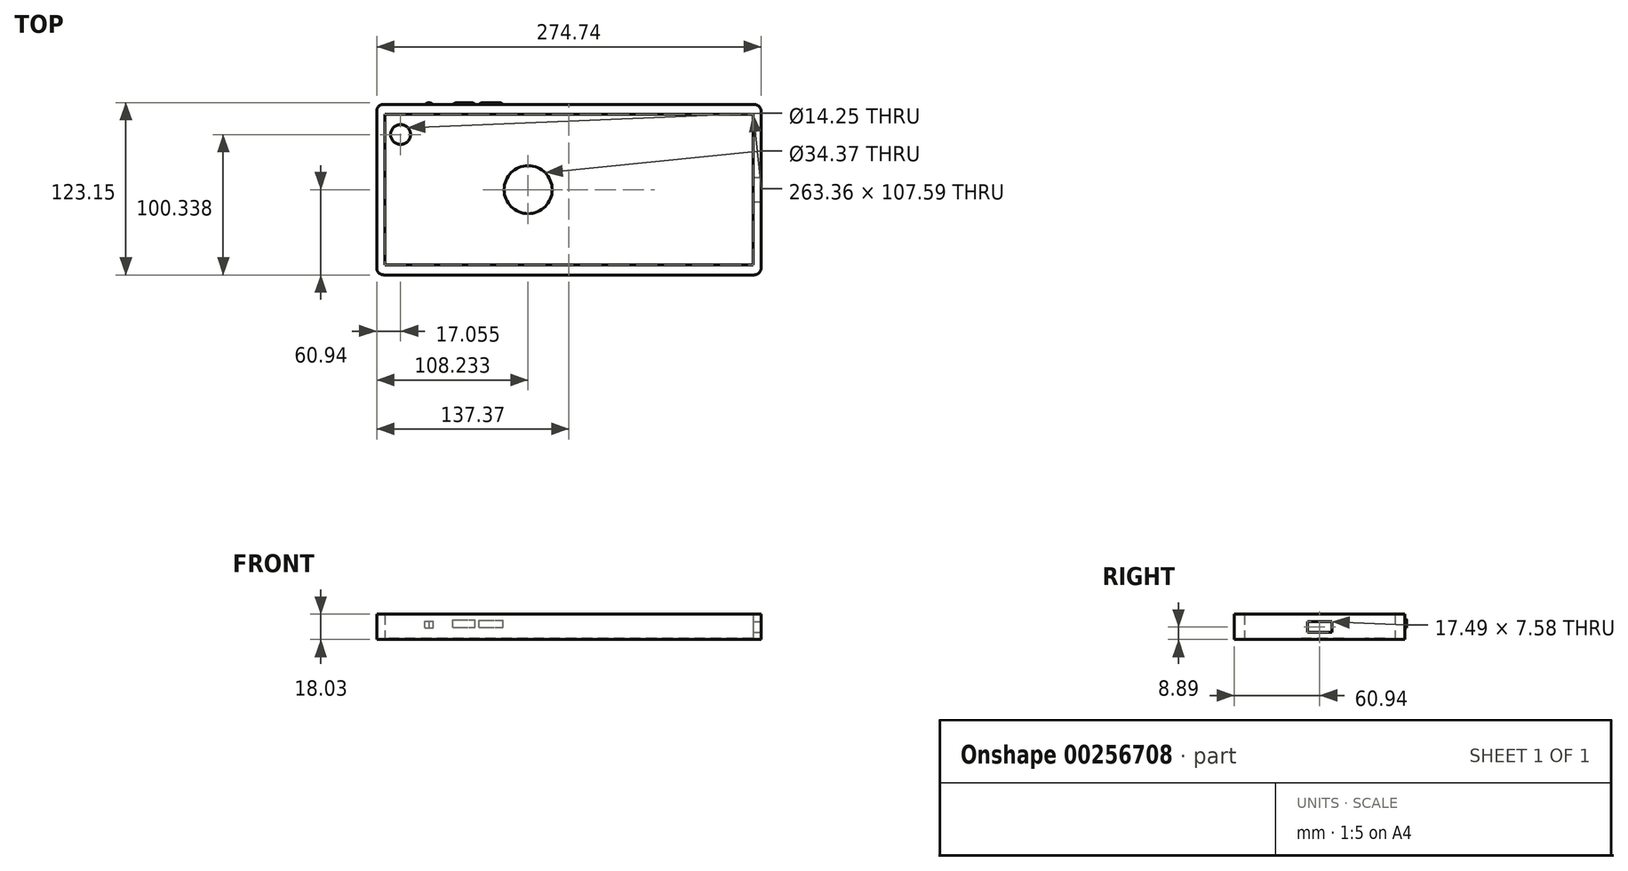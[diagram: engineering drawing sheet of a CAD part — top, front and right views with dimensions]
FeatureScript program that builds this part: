
annotation { "Feature Type Name" : "Feature", "Feature Type Description" : "" }
export const myFeature = defineFeature(function(context is Context, id is Id, definition is map)
    precondition{}
    {
        {
            var Q0;
            Q0=qCreatedBy(makeId("Top.planeOp"),FACE);
            var sketch = newSketch(context, id + "F0", { "sketchPlane" : qUnion([Q0])});
            skLineSegment(sketch, "E0.bottom", {"start": v(137.37, -60.94) * mm, "end": v(-137.37, -60.94) * mm});
            skLineSegment(sketch, "E0.top", {"start": v(137.37, 60.94) * mm, "end": v(-137.37, 60.94) * mm});
            skLineSegment(sketch, "E0.left", {"start": v(137.37, -60.94) * mm, "end": v(137.37, 60.94) * mm});
            skLineSegment(sketch, "E0.right", {"start": v(-137.37, -60.94) * mm, "end": v(-137.37, 60.94) * mm});
            skPoint(sketch, "E0.middle", {"position": v(0, 0) * mm});
            skLineSegment(sketch, "E1.bottom", {"start": v(131.68, -53.8) * mm, "end": v(-131.68, -53.8) * mm});
            skLineSegment(sketch, "E1.top", {"start": v(131.68, 53.8) * mm, "end": v(-131.68, 53.8) * mm});
            skLineSegment(sketch, "E1.left", {"start": v(131.68, -53.8) * mm, "end": v(131.68, 53.8) * mm});
            skLineSegment(sketch, "E1.right", {"start": v(-131.68, -53.8) * mm, "end": v(-131.68, 53.8) * mm});
            skSolve(sketch);
        }
        {
            var Q0;
            Q0 = qSketchRegion(id + "F0", true);
            extrude(context, id + "F1", {"entities" : qUnion([Q0]), "depth" : 18.03 * mm});
        }
        {
            var Q0;
            Q0=makeQuery(id+"F1.opExtrude","CAP_FACE",FACE,{"disambiguationData":[OSD([sQuery(id+"F0.wireOp",EDGE,"E0.bottom"),sQuery(id+"F0.wireOp",EDGE,"E0.top"),sQuery(id+"F0.wireOp",EDGE,"E0.left"),sQuery(id+"F0.wireOp",EDGE,"E0.right"),sQuery(id+"F0.wireOp",EDGE,"E1.bottom"),sQuery(id+"F0.wireOp",EDGE,"E1.top"),sQuery(id+"F0.wireOp",EDGE,"E1.left"),sQuery(id+"F0.wireOp",EDGE,"E1.right")])],"isStart":true});
            var sketch = newSketch(context, id + "F2", { "sketchPlane" : qUnion([Q0])});
            skLineSegment(sketch, "E2.bottom", {"start": v(131.68, -53.8) * mm, "end": v(-131.68, -53.8) * mm});
            skLineSegment(sketch, "E2.top", {"start": v(131.68, 53.8) * mm, "end": v(-131.68, 53.8) * mm});
            skLineSegment(sketch, "E2.left", {"start": v(131.68, -53.8) * mm, "end": v(131.68, 53.8) * mm});
            skLineSegment(sketch, "E2.right", {"start": v(-131.68, -53.8) * mm, "end": v(-131.68, 53.8) * mm});
            skPoint(sketch, "E2.middle", {"position": v(0, 0) * mm});
            skCircle(sketch, "E3", {"center": v(-29.14, 0) * mm, "radius": 17.19 * mm});
            skCircle(sketch, "E4", {"center": v(-120.31, -39.4) * mm, "radius": 7.13 * mm});
            skSolve(sketch);
        }
        {
            var Q0;
            Q0=makeQuery(id+"F2.imprint","IMPRINT",FACE,{"disambiguationData":[TD([[makeQuery(id+"F2.imprint","IMPRINT",EDGE,{"derivedFrom":sQuery(id+"F2.wireOp",EDGE,"E2.bottom")}),-1.0]])]});
            extrude(context, id + "F3", {"entities" : qUnion([Q0]), "oppositeDirection" : true, "depth" : 0.76 * mm});
        }
        {
            var Q0;
            Q0=makeQuery(id+"F1.opExtrude","SWEPT_FACE",FACE,{"disambiguationData":[OSD([sQuery(id+"F0.wireOp",EDGE,"E0.left")])]});
            var sketch = newSketch(context, id + "F4", { "sketchPlane" : qUnion([Q0])});
            skLineSegment(sketch, "E5.bottom", {"start": v(8.74, 5.1) * mm, "end": v(-8.74, 5.1) * mm});
            skLineSegment(sketch, "E5.top", {"start": v(8.74, 12.68) * mm, "end": v(-8.74, 12.68) * mm});
            skLineSegment(sketch, "E5.left", {"start": v(8.74, 5.1) * mm, "end": v(8.74, 12.68) * mm});
            skLineSegment(sketch, "E5.right", {"start": v(-8.74, 5.1) * mm, "end": v(-8.74, 12.68) * mm});
            skPoint(sketch, "E5.middle", {"position": v(0, 8.9) * mm});
            skSolve(sketch);
        }
        {
            var Q0;
            Q0=makeQuery(id+"F4.imprint","IMPRINT",FACE,{"disambiguationData":[TD([[makeQuery(id+"F4.imprint","IMPRINT",EDGE,{"derivedFrom":sQuery(id+"F4.wireOp",EDGE,"E5.bottom")}),-1.0]])]});
            extrude(context, id + "F5", {"entities" : qUnion([Q0]), "operationType" : NewBodyOperationType.REMOVE, "oppositeDirection" : true, "depth" : 25.4 * mm});
        }
        {
            var Q0;
            Q0=makeQuery(id+"F1.opExtrude","SWEPT_FACE",FACE,{"disambiguationData":[OSD([sQuery(id+"F0.wireOp",EDGE,"E0.top")])]});
            var sketch = newSketch(context, id + "F6", { "sketchPlane" : qUnion([Q0])});
            skLineSegment(sketch, "E6.bottom", {"start": v(64.37, 8.6) * mm, "end": v(47.01, 8.6) * mm});
            skLineSegment(sketch, "E6.top", {"start": v(64.37, 13.82) * mm, "end": v(47.01, 13.82) * mm});
            skLineSegment(sketch, "E6.left", {"start": v(64.37, 8.6) * mm, "end": v(64.37, 13.82) * mm});
            skLineSegment(sketch, "E6.right", {"start": v(47.01, 8.6) * mm, "end": v(47.01, 13.82) * mm});
            skPoint(sketch, "E6.middle", {"position": v(55.7, 11.22) * mm});
            skLineSegment(sketch, "E7.bottom", {"start": v(82.97, 8.6) * mm, "end": v(66.92, 8.6) * mm});
            skLineSegment(sketch, "E7.top", {"start": v(82.97, 14.11) * mm, "end": v(66.92, 14.11) * mm});
            skLineSegment(sketch, "E7.left", {"start": v(82.97, 8.6) * mm, "end": v(82.97, 14.11) * mm});
            skLineSegment(sketch, "E7.right", {"start": v(66.92, 8.6) * mm, "end": v(66.92, 14.11) * mm});
            skPoint(sketch, "E7.middle", {"position": v(74.94, 11.35) * mm});
            skLineSegment(sketch, "E8.bottom", {"start": v(102.9, 8.33) * mm, "end": v(97.08, 8.33) * mm});
            skLineSegment(sketch, "E8.top", {"start": v(102.9, 13.21) * mm, "end": v(97.08, 13.21) * mm});
            skLineSegment(sketch, "E8.left", {"start": v(102.9, 8.33) * mm, "end": v(102.9, 13.21) * mm});
            skLineSegment(sketch, "E8.right", {"start": v(97.08, 8.33) * mm, "end": v(97.08, 13.21) * mm});
            skPoint(sketch, "E8.middle", {"position": v(100, 10.77) * mm});
            skSolve(sketch);
        }
        {
            var Q0;
            Q0 = qSketchRegion(id + "F6", true);
            extrude(context, id + "F7", {"entities" : qUnion([Q0]), "operationType" : NewBodyOperationType.ADD, "depth" : 1.27 * mm});
        }
        {
            var Q0;
            Q0=makeQuery(id+"F7.opExtrude","CAP_EDGE",EDGE,{"disambiguationData":[OSD([sQuery(id+"F6.wireOp",EDGE,"E6.right")])],"isStart":false});
            var Q1;
            Q1=makeQuery(id+"F7.opExtrude","CAP_EDGE",EDGE,{"disambiguationData":[OSD([sQuery(id+"F6.wireOp",EDGE,"E6.left")])],"isStart":false});
            var Q2;
            Q2=makeQuery(id+"F7.opExtrude","CAP_EDGE",EDGE,{"disambiguationData":[OSD([sQuery(id+"F6.wireOp",EDGE,"E7.right")])],"isStart":false});
            var Q3;
            Q3=makeQuery(id+"F7.opExtrude","CAP_EDGE",EDGE,{"disambiguationData":[OSD([sQuery(id+"F6.wireOp",EDGE,"E7.left")])],"isStart":false});
            var Q4;
            Q4=makeQuery(id+"F7.opExtrude","CAP_EDGE",EDGE,{"disambiguationData":[OSD([sQuery(id+"F6.wireOp",EDGE,"E8.left")])],"isStart":false});
            var Q5;
            Q5=makeQuery(id+"F7.opExtrude","CAP_EDGE",EDGE,{"disambiguationData":[OSD([sQuery(id+"F6.wireOp",EDGE,"E8.right")])],"isStart":false});
            fillet(context, id + "F8", {"entities" : qUnion([Q0, Q1, Q2, Q3, Q4, Q5]), "radius" : 5.08 * mm, "tangentPropagation" : true, "allowEdgeOverflow" : false});
        }
        {
            var Q0;
            Q0=makeQuery(id+"F1.opExtrude","SWEPT_EDGE",EDGE,{"disambiguationData":[OSD([sQuery(id+"F0.wireOp",EDGE,"E0.top"),sQuery(id+"F0.wireOp",EDGE,"E0.right")])]});
            var Q1;
            Q1=makeQuery(id+"F1.opExtrude","SWEPT_EDGE",EDGE,{"disambiguationData":[OSD([sQuery(id+"F0.wireOp",EDGE,"E0.top"),sQuery(id+"F0.wireOp",EDGE,"E0.left")])]});
            var Q2;
            Q2=makeQuery(id+"F1.opExtrude","SWEPT_EDGE",EDGE,{"disambiguationData":[OSD([sQuery(id+"F0.wireOp",EDGE,"E0.bottom"),sQuery(id+"F0.wireOp",EDGE,"E0.left")])]});
            var Q3;
            Q3=makeQuery(id+"F1.opExtrude","SWEPT_EDGE",EDGE,{"disambiguationData":[OSD([sQuery(id+"F0.wireOp",EDGE,"E0.bottom"),sQuery(id+"F0.wireOp",EDGE,"E0.right")])]});
            fillet(context, id + "F9", {"entities" : qUnion([Q0, Q1, Q2, Q3]), "radius" : 5.08 * mm, "tangentPropagation" : true, "allowEdgeOverflow" : false});
        }
        {
            var Q0;
            Q0=makeQuery(id+"F3.opExtrude","CAP_FACE",FACE,{"disambiguationData":[OSD([sQuery(id+"F2.wireOp",EDGE,"E2.bottom"),sQuery(id+"F2.wireOp",EDGE,"E2.top"),sQuery(id+"F2.wireOp",EDGE,"E2.left"),sQuery(id+"F2.wireOp",EDGE,"E2.right"),sQuery(id+"F2.wireOp",EDGE,"E3"),sQuery(id+"F2.wireOp",EDGE,"E4")])],"isStart":true});
            var sketch = newSketch(context, id + "F10", { "sketchPlane" : qUnion([Q0])});
            skCircle(sketch, "E9", {"center": v(-40.56, 17.53) * mm, "radius": 9.05 * mm});
            skSolve(sketch);
        }
        {
            var Q0;
            {var subQ0=sQuery(id+"F10.wireOp",EDGE,"E9");var subQ1=makeQuery(id+"F3.opExtrude","CAP_EDGE",EDGE,{"disambiguationData":[OSD([sQuery(id+"F2.wireOp",EDGE,"E3")])],"isStart":true});var subQ2=makeQuery(id+"F10.imprint","INTERSECT",VERTEX,{"disambiguationData":[OD(0.0)],"derivedFrom":[subQ1,subQ0]});Q0=makeQuery(id+"F10.imprint","IMPRINT",FACE,{"disambiguationData":[TD([[makeQuery(id+"F10.imprint","IMPRINT",EDGE,{"disambiguationData":[TD([[subQ2,-1.0]])],"derivedFrom":subQ0}),1.0]])]});}
            extrude(context, id + "F11", {"entities" : qUnion([Q0]), "operationType" : NewBodyOperationType.REMOVE, "depth" : 151.38 * mm});
        }
    });
